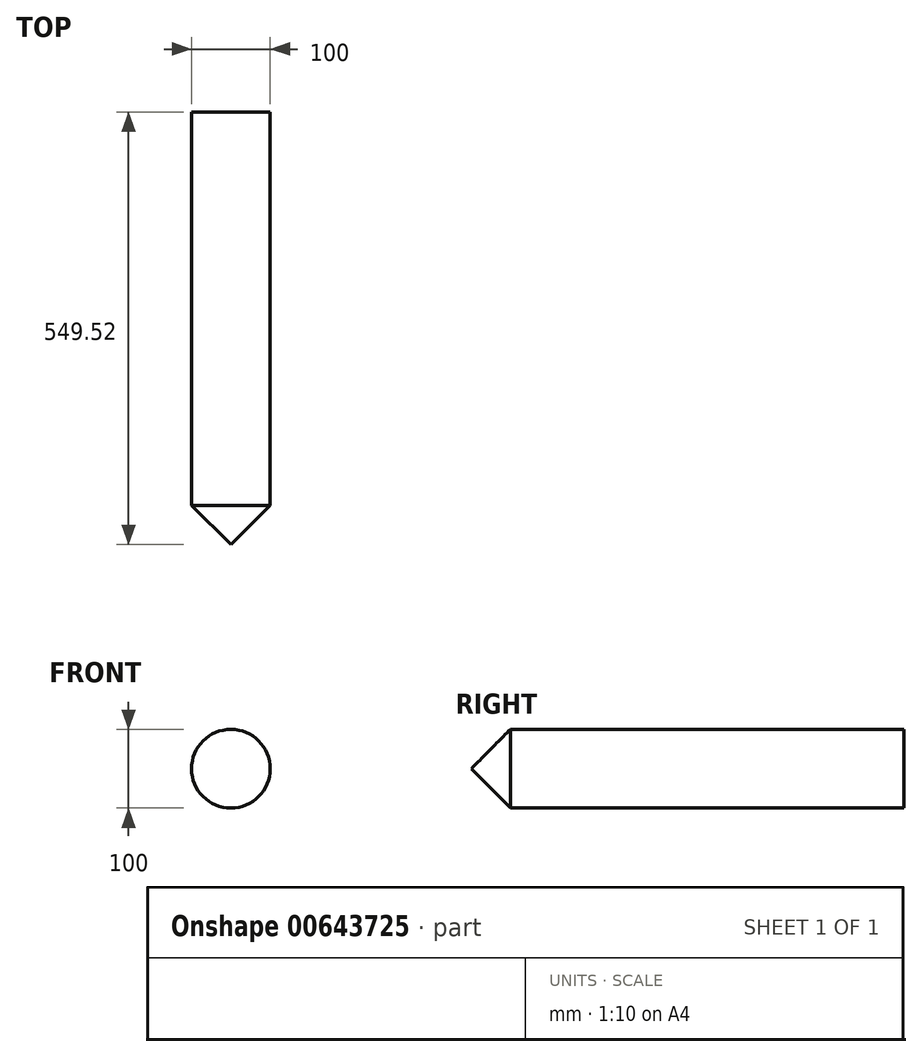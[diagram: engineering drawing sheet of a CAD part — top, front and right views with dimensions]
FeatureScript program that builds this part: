
annotation { "Feature Type Name" : "Feature", "Feature Type Description" : "" }
export const myFeature = defineFeature(function(context is Context, id is Id, definition is map)
    precondition{}
    {
        {
            var Q0;
            Q0=qCreatedBy(makeId("Front.planeOp"),FACE);
            var sketch = newSketch(context, id + "F0", { "sketchPlane" : qUnion([Q0])});
            skCircle(sketch, "E0", {"center": v(0, 0) * mm, "radius": 50 * mm});
            skSolve(sketch);
        }
        {
            var Q0;
            Q0 = qSketchRegion(id + "F0", true);
            extrude(context, id + "F1", {"entities" : qUnion([Q0]), "depth" : 500 * mm, "offsetDistance" : 25 * mm});
        }
        {
            var Q0;
            Q0=qCreatedBy(makeId("Right.planeOp"),FACE);
            var sketch = newSketch(context, id + "F2", { "sketchPlane" : qUnion([Q0])});
            skLineSegment(sketch, "E1", {"start": v(0, 0) * mm, "end": v(-549.52, 0) * mm});
            skLineSegment(sketch, "E2.0", {"start": v(-500, -50) * mm, "end": v(-500, 50) * mm});
            skLineSegment(sketch, "E3", {"start": v(-549.52, 0) * mm, "end": v(-500, 50) * mm});
            skSolve(sketch);
        }
        {
            var Q0;
            {var subQ0=sQuery(id+"F2.wireOp",EDGE,"E3");Q0=makeQuery(id+"F2.imprint","IMPRINT",FACE,{"disambiguationData":[TD([[makeQuery(id+"F2.imprint","IMPRINT",EDGE,{"derivedFrom":subQ0}),-1.0]])]});}
            var Q1;
            Q1=sQuery(id+"F2.wireOp",EDGE,"E1");
            revolve(context, id + "F3", {"operationType" : NewBodyOperationType.ADD, "entities" : qUnion([Q0]), "axis" : qUnion([Q1]), "revolveType" : RevolveType.FULL});
        }
    });
